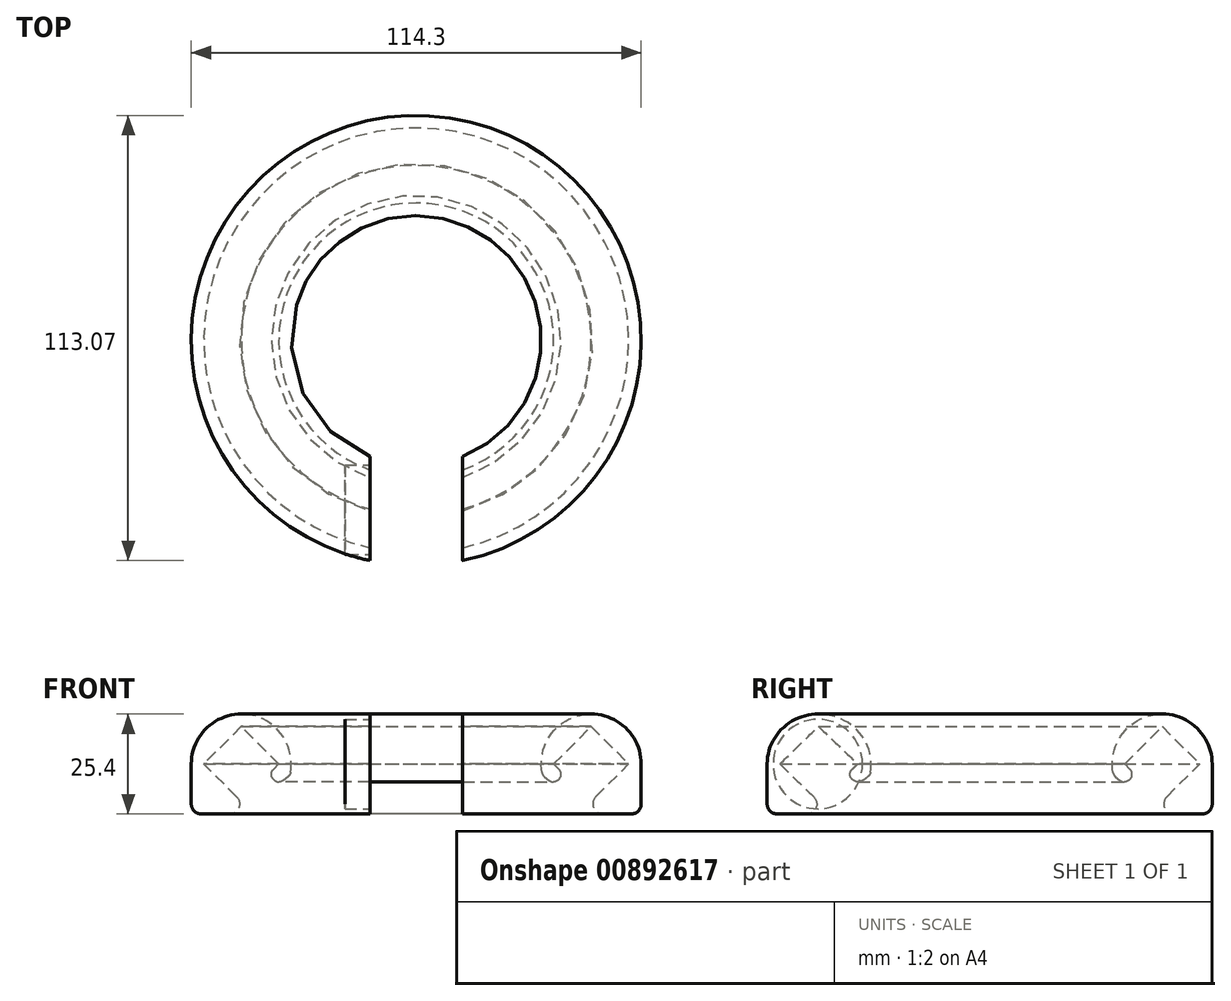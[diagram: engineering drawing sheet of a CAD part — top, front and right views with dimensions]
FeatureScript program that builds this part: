
annotation { "Feature Type Name" : "Feature", "Feature Type Description" : "" }
export const myFeature = defineFeature(function(context is Context, id is Id, definition is map)
    precondition{}
    {
        {
            var Q0;
            Q0=qCreatedBy(makeId("Front.planeOp"),FACE);
            var sketch = newSketch(context, id + "F0", { "sketchPlane" : qUnion([Q0])});
            skLineSegment(sketch, "E0", {"start": v(0, 0) * mm, "end": v(-31.75, 0) * mm, "construction": true});
            skLineSegment(sketch, "E1", {"start": v(-31.75, 0) * mm, "end": v(-44.45, 0) * mm, "construction": true});
            skCircle(sketch, "E2", {"center": v(-44.45, 0) * mm, "radius": 12.7 * mm});
            skLineSegment(sketch, "E3", {"start": v(-57.15, 0) * mm, "end": v(-57.15, -12.7) * mm});
            skLineSegment(sketch, "E4", {"start": v(-31.75, 0) * mm, "end": v(-31.75, -12.7) * mm});
            skLineSegment(sketch, "E5", {"start": v(-57.15, -12.7) * mm, "end": v(-31.75, -12.7) * mm});
            skLineSegment(sketch, "E6", {"start": v(-44.45, 0) * mm, "end": v(-53.98, 0) * mm});
            skLineSegment(sketch, "E7", {"start": v(-44.45, 0) * mm, "end": v(-34.93, 0) * mm});
            skLineSegment(sketch, "E8", {"start": v(-44.45, 0) * mm, "end": v(-44.45, 9.52) * mm});
            skLineSegment(sketch, "E9", {"start": v(-44.45, 0) * mm, "end": v(-44.45, -9.53) * mm});
            skLineSegment(sketch, "E10", {"start": v(-53.98, 0) * mm, "end": v(-44.45, 9.52) * mm});
            skLineSegment(sketch, "E11", {"start": v(-44.45, 9.52) * mm, "end": v(-34.93, 0) * mm});
            skLineSegment(sketch, "E12", {"start": v(-44.45, -9.53) * mm, "end": v(-34.93, 0) * mm});
            skLineSegment(sketch, "E13", {"start": v(-53.98, 0) * mm, "end": v(-44.45, -9.53) * mm});
            skLineSegment(sketch, "E14", {"start": v(-34.93, 0) * mm, "end": v(-28.47, -6.46) * mm});
            skLineSegment(sketch, "E15", {"start": v(-44.45, -9.53) * mm, "end": v(-38.47, -15.5) * mm});
            skLineSegment(sketch, "E16", {"start": v(-38.47, -15.5) * mm, "end": v(-28.47, -6.46) * mm});
            skLineSegment(sketch, "E17", {"start": v(0, 0) * mm, "end": v(0, 25.96) * mm});
            skLineSegment(sketch, "E18", {"start": v(-34.93, 0) * mm, "end": v(-37.62, -2.7) * mm});
            skLineSegment(sketch, "E19", {"start": v(-34.93, 0) * mm, "end": v(-34.93, -5.08) * mm});
            skLineSegment(sketch, "E20", {"start": v(-34.93, -5.08) * mm, "end": v(-37.62, -2.7) * mm});
            skLineSegment(sketch, "E21", {"start": v(-34.93, -5.08) * mm, "end": v(-32.07, -2.85) * mm});
            skSolve(sketch);
        }
        {
            var Q0;
            {var subQ0=sQuery(id+"F0.wireOp",EDGE,"E3");Q0=makeQuery(id+"F0.imprint","IMPRINT",FACE,{"disambiguationData":[TD([[makeQuery(id+"F0.imprint","IMPRINT",EDGE,{"derivedFrom":subQ0}),1.0]])]});}
            var Q1;
            Q1=makeQuery(id+"F0.imprint","IMPRINT",FACE,{"disambiguationData":[TD([[makeQuery(id+"F0.imprint","IMPRINT",EDGE,{"derivedFrom":sQuery(id+"F0.wireOp",EDGE,"E10")}),1.0]])]});
            var Q2;
            {var subQ0=sQuery(id+"F0.wireOp",EDGE,"E19");Q2=makeQuery(id+"F0.imprint","IMPRINT",FACE,{"disambiguationData":[TD([[makeQuery(id+"F0.imprint","IMPRINT",EDGE,{"derivedFrom":subQ0}),-1.0]])]});}
            var Q3;
            {var subQ0=sQuery(id+"F0.wireOp",EDGE,"E19");Q3=makeQuery(id+"F0.imprint","IMPRINT",FACE,{"disambiguationData":[TD([[makeQuery(id+"F0.imprint","IMPRINT",EDGE,{"derivedFrom":subQ0}),1.0]])]});}
            var Q4;
            Q4=sQuery(id+"F0.wireOp",EDGE,"E17");
            revolve(context, id + "F1", {"surfaceOperationType" : NewSurfaceOperationType.NEW, "entities" : qUnion([Q0, Q1, Q2, Q3]), "axis" : qUnion([Q4]), "revolveType" : RevolveType.FULL});
        }
        {
            var Q0;
            Q0=makeQuery(id+"F1.opRevolve","SWEPT_EDGE",EDGE,{"disambiguationData":[OSD([sQuery(id+"F0.wireOp",EDGE,"E3"),sQuery(id+"F0.wireOp",EDGE,"E5")])]});
            var Q1;
            Q1=makeQuery(id+"F1.opRevolve","SWEPT_EDGE",EDGE,{"disambiguationData":[OSD([sQuery(id+"F0.wireOp",EDGE,"E2"),sQuery(id+"F0.wireOp",EDGE,"E15")])]});
            fillet(context, id + "F2", {"entities" : qUnion([Q0, Q1]), "radius" : 2.54 * mm, "tangentPropagation" : true, "allowEdgeOverflow" : false});
        }
        {
            var Q0;
            Q0=makeQuery(id+"F1.opRevolve","SWEPT_EDGE",EDGE,{"disambiguationData":[OSD([sQuery(id+"F0.wireOp",EDGE,"E12"),sQuery(id+"F0.wireOp",EDGE,"E20")])]});
            var Q1;
            Q1=makeQuery(id+"F1.opRevolve","SWEPT_EDGE",EDGE,{"disambiguationData":[OSD([sQuery(id+"F0.wireOp",EDGE,"E19"),sQuery(id+"F0.wireOp",EDGE,"E20"),sQuery(id+"F0.wireOp",EDGE,"E21")])]});
            var Q2;
            Q2=makeQuery(id+"F1.opRevolve","SWEPT_EDGE",EDGE,{"disambiguationData":[OSD([sQuery(id+"F0.wireOp",EDGE,"E2"),sQuery(id+"F0.wireOp",EDGE,"E14"),sQuery(id+"F0.wireOp",EDGE,"E21")])]});
            fillet(context, id + "F3", {"entities" : qUnion([Q0, Q1, Q2]), "radius" : 1.78 * mm, "tangentPropagation" : true, "allowEdgeOverflow" : false});
        }
        {
            var Q0;
            Q0=qCreatedBy(makeId("Front.planeOp"),FACE);
            cPlane(context, id + "F4", {"entities" : qUnion([Q0]), "cplaneType" : CPlaneType.OFFSET, "offset" : 57.4 * mm, "width" : 152.4 * mm, "height" : 152.4 * mm});
        }
        {
            var Q0;
            Q0=qCreatedBy(id+"F4.planeOp",FACE);
            var sketch = newSketch(context, id + "F5", { "sketchPlane" : qUnion([Q0])});
            skLineSegment(sketch, "E22.bottom", {"start": v(11.79, -19.33) * mm, "end": v(-11.79, -19.33) * mm});
            skLineSegment(sketch, "E22.top", {"start": v(11.79, 19.33) * mm, "end": v(-11.79, 19.33) * mm});
            skLineSegment(sketch, "E22.left", {"start": v(11.79, -19.33) * mm, "end": v(11.79, 19.33) * mm});
            skLineSegment(sketch, "E22.right", {"start": v(-11.79, -19.33) * mm, "end": v(-11.79, 19.33) * mm});
            skPoint(sketch, "E22.middle", {"position": v(0, 0) * mm});
            skSolve(sketch);
        }
        {
            var Q0;
            Q0=makeQuery(id+"F5.imprint","IMPRINT",FACE,{"disambiguationData":[TD([[makeQuery(id+"F5.imprint","IMPRINT",EDGE,{"derivedFrom":sQuery(id+"F5.wireOp",EDGE,"E22.bottom")}),-1.0]])]});
            extrude(context, id + "F6", {"entities" : qUnion([Q0]), "operationType" : NewBodyOperationType.REMOVE, "oppositeDirection" : true, "depth" : 33.02 * mm, "offsetDistance" : 25.4 * mm});
        }
        {
            var Q0;
            Q0=makeQuery(id+"F6.boolean.opBoolean","COPY",FACE,{"derivedFrom":makeQuery(id+"F6.opExtrude","SWEPT_FACE",FACE,{"disambiguationData":[OSD([sQuery(id+"F5.wireOp",EDGE,"E22.right")])]})});
            var sketch = newSketch(context, id + "F7", { "sketchPlane" : qUnion([Q0])});
            skLineSegment(sketch, "E23", {"start": v(-52.67, 0) * mm, "end": v(-43.02, 0) * mm});
            skCircle(sketch, "E24", {"center": v(-43.02, 0) * mm, "radius": 11.35 * mm});
            skSolve(sketch);
        }
        {
            var Q0;
            {var subQ0=makeQuery(id+"F6.opExtrude","SWEPT_FACE",FACE,{"disambiguationData":[OSD([sQuery(id+"F5.wireOp",EDGE,"E22.right")])]});Q0=makeQuery(id+"F7.imprint","IMPRINT",FACE,{"disambiguationData":[TD([[makeQuery(id+"F7.imprint","IMPRINT",EDGE,{"derivedFrom":makeQuery(id+"F6.boolean.opBoolean","INTERSECT",EDGE,{"derivedFrom":[makeQuery(id+"F1.opRevolve","SWEPT_FACE",FACE,{"disambiguationData":[OSD([sQuery(id+"F0.wireOp",EDGE,"E10")])]}),subQ0]})}),-1.0]])]});}
            var Q1;
            {var subQ0=makeQuery(id+"F6.opExtrude","SWEPT_FACE",FACE,{"disambiguationData":[OSD([sQuery(id+"F5.wireOp",EDGE,"E22.right")])]});Q1=makeQuery(id+"F7.imprint","IMPRINT",FACE,{"disambiguationData":[TD([[makeQuery(id+"F7.imprint","IMPRINT",EDGE,{"derivedFrom":makeQuery(id+"F6.boolean.opBoolean","INTERSECT",EDGE,{"derivedFrom":[makeQuery(id+"F1.opRevolve","SWEPT_FACE",FACE,{"disambiguationData":[OSD([sQuery(id+"F0.wireOp",EDGE,"E10")])]}),subQ0]})}),1.0]])]});}
            extrude(context, id + "F8", {"entities" : qUnion([Q0, Q1]), "oppositeDirection" : true, "depth" : 6.35 * mm, "offsetDistance" : 25.4 * mm});
        }
    });
